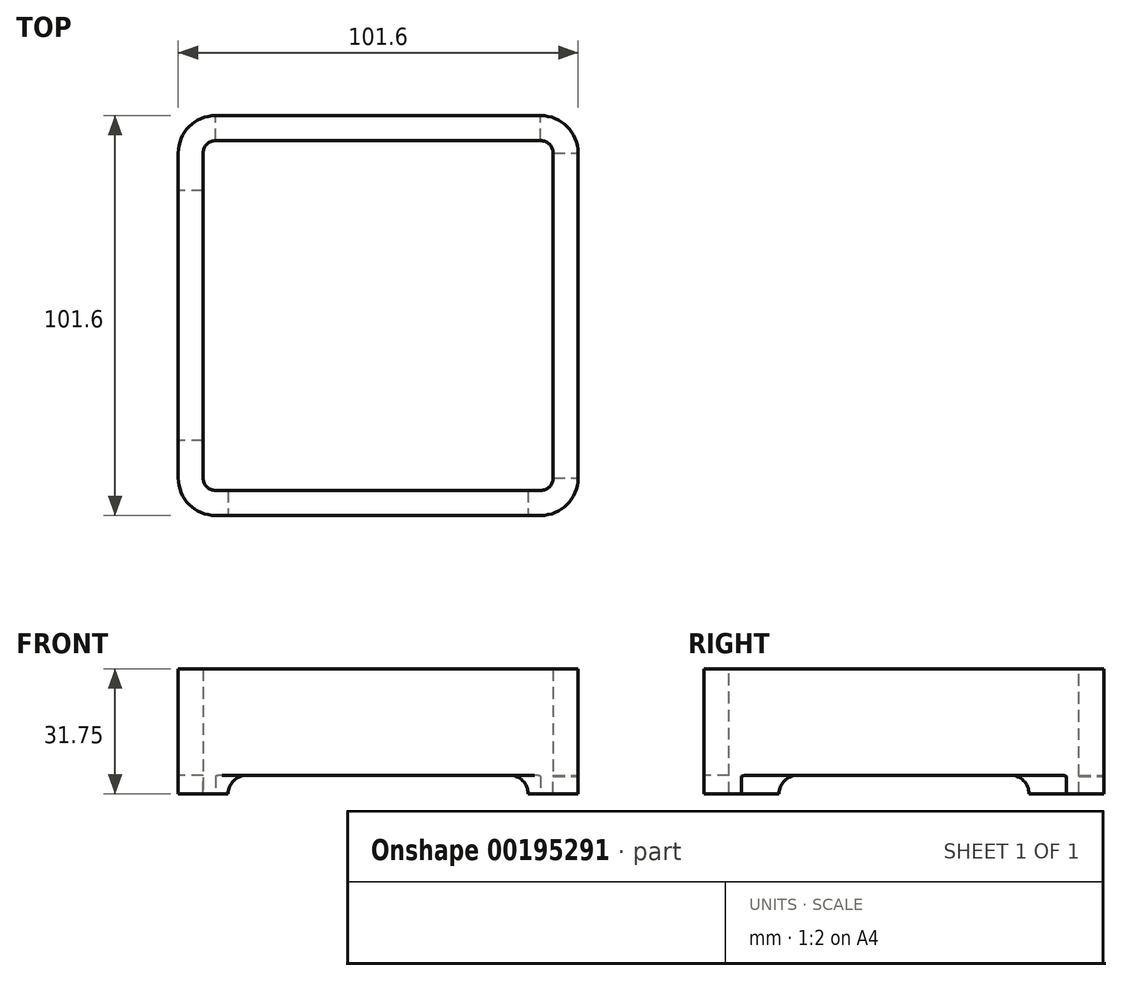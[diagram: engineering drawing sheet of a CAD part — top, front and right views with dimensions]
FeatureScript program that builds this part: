
annotation { "Feature Type Name" : "Feature", "Feature Type Description" : "" }
export const myFeature = defineFeature(function(context is Context, id is Id, definition is map)
    precondition{}
    {
        {
            var Q0;
            Q0=qCreatedBy(makeId("Top.planeOp"),FACE);
            var sketch = newSketch(context, id + "F0", { "sketchPlane" : qUnion([Q0])});
            skLineSegment(sketch, "E0.bottom", {"start": v(0, 0) * mm, "end": v(101.6, 0) * mm});
            skLineSegment(sketch, "E0.top", {"start": v(0, -101.6) * mm, "end": v(101.6, -101.6) * mm});
            skLineSegment(sketch, "E0.left", {"start": v(0, 0) * mm, "end": v(0, -101.6) * mm});
            skLineSegment(sketch, "E0.right", {"start": v(101.6, 0) * mm, "end": v(101.6, -101.6) * mm});
            skSolve(sketch);
        }
        {
            var Q0;
            Q0 = qSketchRegion(id + "F0", true);
            extrude(context, id + "F1", {"entities" : qUnion([Q0]), "depth" : 31.75 * mm});
        }
        {
            var Q0;
            Q0=makeQuery(id+"F1.opExtrude","SWEPT_EDGE",EDGE,{"disambiguationData":[OSD([sQuery(id+"F0.wireOp",EDGE,"E0.top"),sQuery(id+"F0.wireOp",EDGE,"E0.left")])]});
            var Q1;
            Q1=makeQuery(id+"F1.opExtrude","SWEPT_EDGE",EDGE,{"disambiguationData":[OSD([sQuery(id+"F0.wireOp",EDGE,"E0.bottom"),sQuery(id+"F0.wireOp",EDGE,"E0.left")])]});
            var Q2;
            Q2=makeQuery(id+"F1.opExtrude","SWEPT_EDGE",EDGE,{"disambiguationData":[OSD([sQuery(id+"F0.wireOp",EDGE,"E0.bottom"),sQuery(id+"F0.wireOp",EDGE,"E0.right")])]});
            var Q3;
            Q3=makeQuery(id+"F1.opExtrude","SWEPT_EDGE",EDGE,{"disambiguationData":[OSD([sQuery(id+"F0.wireOp",EDGE,"E0.top"),sQuery(id+"F0.wireOp",EDGE,"E0.right")])]});
            fillet(context, id + "F2", {"entities" : qUnion([Q0, Q1, Q2, Q3]), "radius" : 9.52 * mm, "tangentPropagation" : true, "allowEdgeOverflow" : false});
        }
        {
            var Q0;
            Q0=makeQuery(id+"F1.opExtrude","CAP_FACE",FACE,{"disambiguationData":[OSD([sQuery(id+"F0.wireOp",EDGE,"E0.bottom"),sQuery(id+"F0.wireOp",EDGE,"E0.top"),sQuery(id+"F0.wireOp",EDGE,"E0.left"),sQuery(id+"F0.wireOp",EDGE,"E0.right")])],"isStart":true});
            var Q1;
            Q1=makeQuery(id+"F1.opExtrude","CAP_FACE",FACE,{"disambiguationData":[OSD([sQuery(id+"F0.wireOp",EDGE,"E0.bottom"),sQuery(id+"F0.wireOp",EDGE,"E0.top"),sQuery(id+"F0.wireOp",EDGE,"E0.left"),sQuery(id+"F0.wireOp",EDGE,"E0.right")])],"isStart":false});
            shell(context, id + "F3", {"entities" : qUnion([Q0, Q1]), "thickness" : 6.35 * mm});
        }
        {
            var Q0;
            Q0=makeQuery(id+"F1.opExtrude","SWEPT_FACE",FACE,{"disambiguationData":[OSD([sQuery(id+"F0.wireOp",EDGE,"E0.top")])]});
            var sketch = newSketch(context, id + "F4", { "sketchPlane" : qUnion([Q0])});
            skPoint(sketch, "E1.orphan", {"position": v(50.8, 31.75) * mm});
            skLineSegment(sketch, "E2", {"start": v(50.8, 4.76) * mm, "end": v(50.8, 0) * mm, "construction": true});
            skLineSegment(sketch, "E3", {"start": v(17.46, 4.76) * mm, "end": v(50.8, 4.76) * mm});
            skArc(sketch, "E4", {"start": v(17.46, 4.76) * mm, "mid": v(14.1, 3.37) * mm, "end": v(12.7, 0) * mm});
            skArc(sketch, "E5.MirrorCS", {"start": v(84.14, 4.76) * mm, "mid": v(87.5, 3.37) * mm, "end": v(88.9, 0) * mm});
            skLineSegment(sketch, "E6.MirrorCS", {"start": v(84.14, 4.76) * mm, "end": v(50.8, 4.76) * mm});
            skSolve(sketch);
        }
        {
            var Q0;
            Q0=makeQuery(id+"F1.opExtrude","SWEPT_FACE",FACE,{"disambiguationData":[OSD([sQuery(id+"F0.wireOp",EDGE,"E0.left")])]});
            var sketch = newSketch(context, id + "F5", { "sketchPlane" : qUnion([Q0])});
            skLineSegment(sketch, "E7", {"start": v(50.8, 4.76) * mm, "end": v(50.8, 0) * mm, "construction": true});
            skLineSegment(sketch, "E8", {"start": v(23.81, 4.76) * mm, "end": v(50.8, 4.76) * mm});
            skArc(sketch, "E9", {"start": v(23.81, 4.76) * mm, "mid": v(20.44, 3.37) * mm, "end": v(19.05, 0) * mm});
            skArc(sketch, "E10.MirrorCS", {"start": v(77.79, 4.76) * mm, "mid": v(81.16, 3.37) * mm, "end": v(82.55, 0) * mm});
            skLineSegment(sketch, "E11.MirrorCS", {"start": v(77.79, 4.76) * mm, "end": v(50.8, 4.76) * mm});
            skPoint(sketch, "E12.orphan", {"position": v(50.8, 31.75) * mm});
            skLineSegment(sketch, "E13", {"start": v(50.8, 0) * mm, "end": v(50.8, 31.75) * mm, "construction": true});
            skSolve(sketch);
        }
        {
            var Q0;
            Q0=makeQuery(id+"F1.opExtrude","SWEPT_FACE",FACE,{"disambiguationData":[OSD([sQuery(id+"F0.wireOp",EDGE,"E0.bottom")])]});
            var sketch = newSketch(context, id + "F6", { "sketchPlane" : qUnion([Q0])});
            skLineSegment(sketch, "E14", {"start": v(-50.8, 4.76) * mm, "end": v(-50.8, 0) * mm, "construction": true});
            skLineSegment(sketch, "E15", {"start": v(-90.49, 4.76) * mm, "end": v(-50.8, 4.76) * mm});
            skArc(sketch, "E16", {"start": v(-90.49, 4.76) * mm, "mid": v(-93.86, 3.37) * mm, "end": v(-95.25, 0) * mm});
            skArc(sketch, "E17.MirrorCS", {"start": v(-11.11, 4.76) * mm, "mid": v(-7.74, 3.37) * mm, "end": v(-6.35, 0) * mm});
            skLineSegment(sketch, "E18.MirrorCS", {"start": v(-11.11, 4.76) * mm, "end": v(-50.8, 4.76) * mm});
            skPoint(sketch, "E19.orphan", {"position": v(-50.8, 31.75) * mm});
            skSolve(sketch);
        }
        {
            var Q0;
            Q0=makeQuery(id+"F1.opExtrude","SWEPT_FACE",FACE,{"disambiguationData":[OSD([sQuery(id+"F0.wireOp",EDGE,"E0.right")])]});
            var sketch = newSketch(context, id + "F7", { "sketchPlane" : qUnion([Q0])});
            skLineSegment(sketch, "E20", {"start": v(-50.8, 4.76) * mm, "end": v(-50.8, 0) * mm, "construction": true});
            skLineSegment(sketch, "E21", {"start": v(-90.49, 4.76) * mm, "end": v(-50.8, 4.76) * mm});
            skArc(sketch, "E22", {"start": v(-90.49, 4.76) * mm, "mid": v(-93.86, 3.37) * mm, "end": v(-95.25, 0) * mm});
            skArc(sketch, "E23.MirrorCS", {"start": v(-11.11, 4.76) * mm, "mid": v(-7.74, 3.37) * mm, "end": v(-6.35, 0) * mm});
            skLineSegment(sketch, "E24.MirrorCS", {"start": v(-11.11, 4.76) * mm, "end": v(-50.8, 4.76) * mm});
            skPoint(sketch, "E25.orphan", {"position": v(-50.8, 31.75) * mm});
            skSolve(sketch);
        }
        {
            var Q0;
            Q0=makeQuery(id+"F6.imprint","IMPRINT",FACE,{"disambiguationData":[TD([[makeQuery(id+"F6.imprint","IMPRINT",EDGE,{"derivedFrom":sQuery(id+"F6.wireOp",EDGE,"E15")}),-1.0]])]});
            extrude(context, id + "F8", {"entities" : qUnion([Q0]), "operationType" : NewBodyOperationType.REMOVE, "endBound" : BoundingType.UP_TO_NEXT, "oppositeDirection" : true, "depth" : 25.4 * mm});
        }
        {
            var Q0;
            Q0=makeQuery(id+"F7.imprint","IMPRINT",FACE,{"disambiguationData":[TD([[makeQuery(id+"F7.imprint","IMPRINT",EDGE,{"derivedFrom":sQuery(id+"F7.wireOp",EDGE,"E21")}),-1.0]])]});
            extrude(context, id + "F9", {"entities" : qUnion([Q0]), "operationType" : NewBodyOperationType.REMOVE, "endBound" : BoundingType.UP_TO_NEXT, "oppositeDirection" : true, "depth" : 25.4 * mm});
        }
        {
            var Q0;
            Q0=makeQuery(id+"F4.imprint","IMPRINT",FACE,{"disambiguationData":[TD([[makeQuery(id+"F4.imprint","IMPRINT",EDGE,{"derivedFrom":sQuery(id+"F4.wireOp",EDGE,"Y4IEfZOl-yBK8-MHtp-5BJy-DPLI7D6EtYrj")}),-1.0]])]});
            var Q1;
            Q1=makeQuery(id+"F4.imprint","IMPRINT",FACE,{"disambiguationData":[TD([[makeQuery(id+"F4.imprint","IMPRINT",EDGE,{"derivedFrom":sQuery(id+"F4.wireOp",EDGE,"E3")}),-1.0]])]});
            extrude(context, id + "F10", {"entities" : qUnion([Q0, Q1]), "operationType" : NewBodyOperationType.REMOVE, "endBound" : BoundingType.UP_TO_NEXT, "oppositeDirection" : true, "depth" : 25.4 * mm});
        }
        {
            var Q0;
            Q0=makeQuery(id+"F5.imprint","IMPRINT",FACE,{"disambiguationData":[TD([[makeQuery(id+"F5.imprint","IMPRINT",EDGE,{"derivedFrom":sQuery(id+"F5.wireOp",EDGE,"E8")}),-1.0]])]});
            extrude(context, id + "F11", {"entities" : qUnion([Q0]), "operationType" : NewBodyOperationType.REMOVE, "endBound" : BoundingType.UP_TO_NEXT, "oppositeDirection" : true, "depth" : 25.4 * mm});
        }
    });
